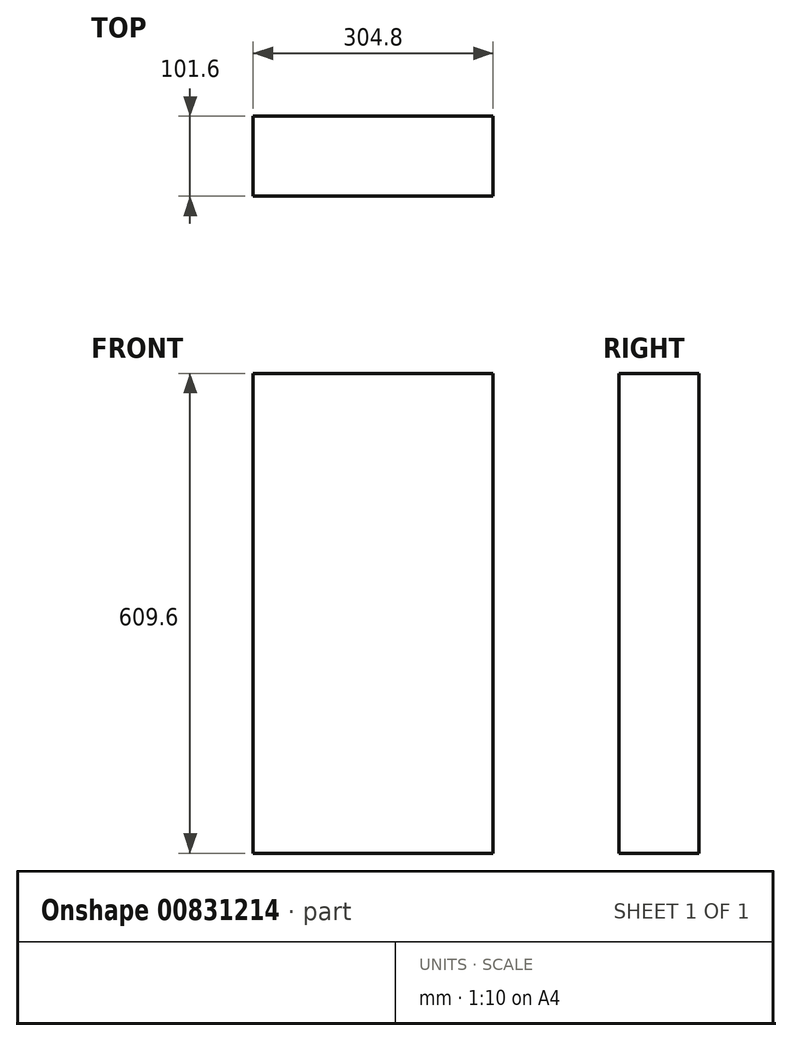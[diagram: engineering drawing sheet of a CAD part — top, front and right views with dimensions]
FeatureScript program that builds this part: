
annotation { "Feature Type Name" : "Feature", "Feature Type Description" : "" }
export const myFeature = defineFeature(function(context is Context, id is Id, definition is map)
    precondition{}
    {
        {
            var Q0;
            Q0=qCreatedBy(makeId("Front.planeOp"),FACE);
            var sketch = newSketch(context, id + "F0", { "sketchPlane" : qUnion([Q0])});
            skLineSegment(sketch, "E0.bottom", {"start": v(152.4, 304.8) * mm, "end": v(-152.4, 304.8) * mm});
            skLineSegment(sketch, "E0.top", {"start": v(152.4, -304.8) * mm, "end": v(-152.4, -304.8) * mm});
            skLineSegment(sketch, "E0.left", {"start": v(152.4, 304.8) * mm, "end": v(152.4, -304.8) * mm});
            skLineSegment(sketch, "E0.right", {"start": v(-152.4, 304.8) * mm, "end": v(-152.4, -304.8) * mm});
            skPoint(sketch, "E0.middle", {"position": v(0, 0) * mm});
            skSolve(sketch);
        }
        {
            var Q0;
            Q0=qSketchRegion(id+"F0",true);
            extrude(context, id + "F1", {"entities" : qUnion([Q0]), "depth" : 101.6 * mm, "offsetDistance" : 25.4 * mm});
        }
    });
